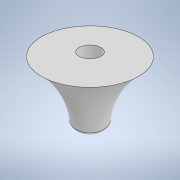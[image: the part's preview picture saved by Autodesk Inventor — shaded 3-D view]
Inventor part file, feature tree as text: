
AUTODESK INVENTOR PART (.ipt)
format: ipt  version: 2022 (Build 260153000, 153)  size: 154,624 bytes
history: native  units: mm
features: sketch x2, revolve x1, fillet x1, projected_geometry x1
ambient origin geometry x8: Origin, YZ Plane, XZ Plane, XY Plane, X Axis, Y Axis, Z Axis, Center Point
bodies: Solid1 (feature_tree)
feature tree (5):
  revolve  "Revolution1"  [1 undecoded]
  fillet  "Fillet1"  Radius=8.0mm
  sketch  "Sketch2"  dims[d3=2.3mm d4=10.0mm d5=2.5mm d6=90.0deg d7=1.0mm]
  sketch  "Sketch1"  dims[d0=1.275mm d1=15.0mm d2=8.0mm]
  projected_geometry  "Projected Loop1"
note: 1 required parameter value undecoded (feature->parameter linkage not recoverable at this tier; creation-order binding heuristic only, values carry confidence <= 0.55)
